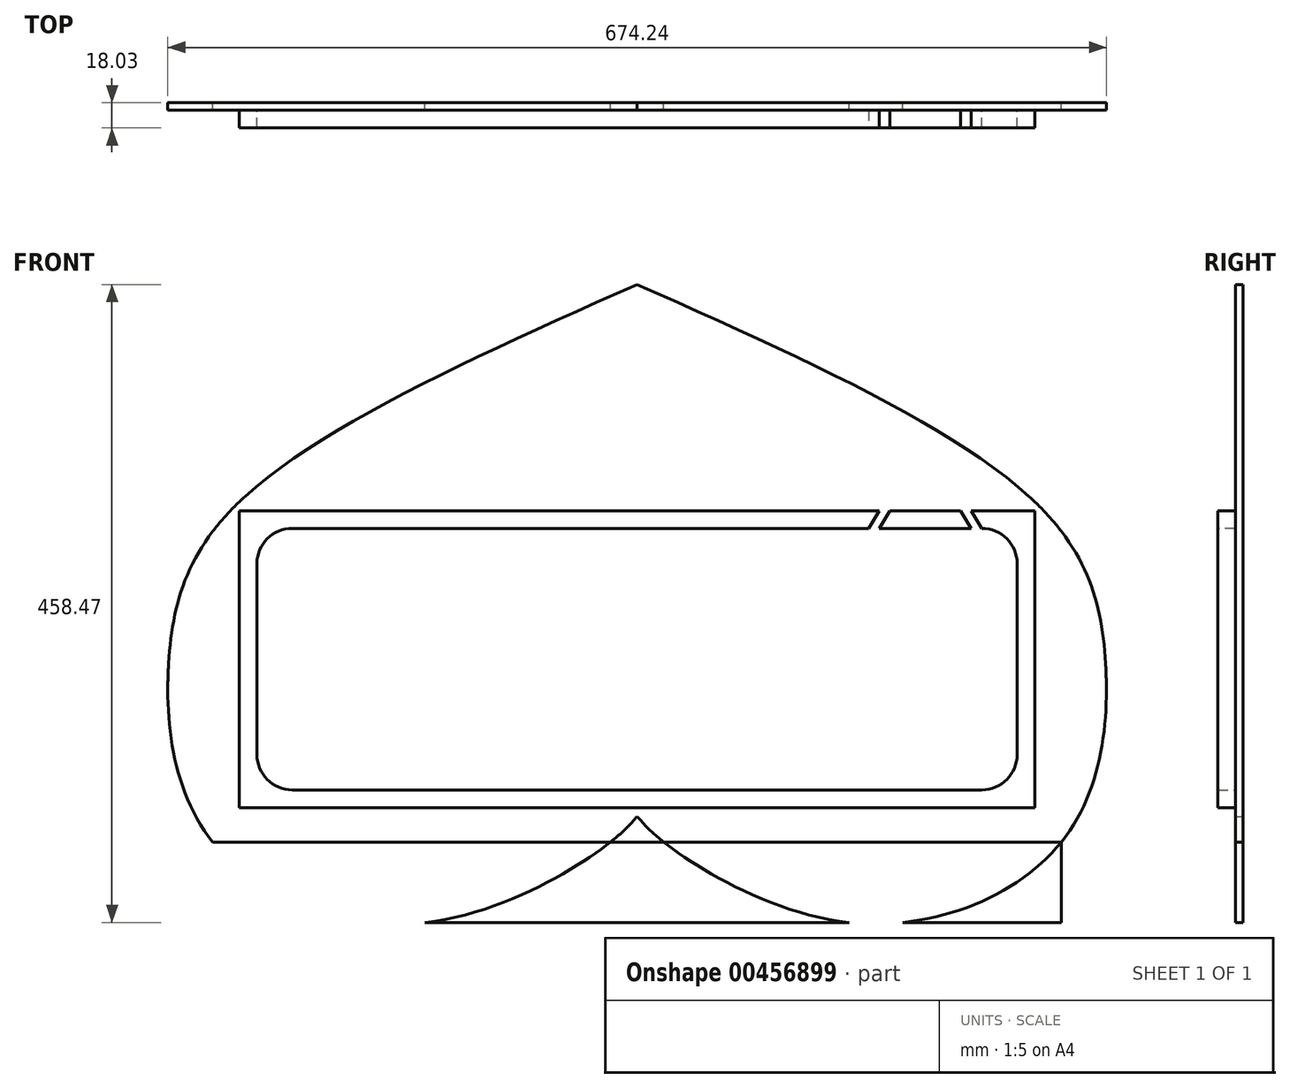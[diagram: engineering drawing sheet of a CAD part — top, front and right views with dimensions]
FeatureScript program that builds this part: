
annotation { "Feature Type Name" : "Feature", "Feature Type Description" : "" }
export const myFeature = defineFeature(function(context is Context, id is Id, definition is map)
    precondition{}
    {
        {
            var Q0;
            Q0=qCreatedBy(makeId("Front.planeOp"),FACE);
            var sketch = newSketch(context, id + "F0", { "sketchPlane" : qUnion([Q0])});
            skLineSegment(sketch, "E0.bottom", {"start": v(0, 0) * mm, "end": v(-584.2, 0) * mm});
            skLineSegment(sketch, "E0.top", {"start": v(0, 219.7) * mm, "end": v(-584.2, 219.7) * mm});
            skLineSegment(sketch, "E0.left", {"start": v(0, 0) * mm, "end": v(0, 219.7) * mm});
            skLineSegment(sketch, "E0.right", {"start": v(-584.2, 0) * mm, "end": v(-584.2, 219.7) * mm});
            skPoint(sketch, "E1", {"position": v(-292.1, 219.7) * mm});
            skSolve(sketch);
        }
        {
            var Q0;
            Q0=makeQuery(id+"F0.imprint","IMPRINT",FACE,{"disambiguationData":[TD([[makeQuery(id+"F0.imprint","IMPRINT",EDGE,{"derivedFrom":sQuery(id+"F0.wireOp",EDGE,"E0.bottom")}),-1.0]])]});
            extrude(context, id + "F1", {"entities" : qUnion([Q0]), "depth" : 5.33 * mm});
        }
        {
            var Q0;
            Q0=makeQuery(id+"F1.opExtrude","CAP_FACE",FACE,{"disambiguationData":[OSD([sQuery(id+"F0.wireOp",EDGE,"E0.bottom"),sQuery(id+"F0.wireOp",EDGE,"E0.top"),sQuery(id+"F0.wireOp",EDGE,"E0.left"),sQuery(id+"F0.wireOp",EDGE,"E0.right")])],"isStart":false});
            var sketch = newSketch(context, id + "F2", { "sketchPlane" : qUnion([Q0])});
            skLineSegment(sketch, "E2", {"start": v(-577.85, 219.7) * mm, "end": v(-577.85, 6.35) * mm});
            skLineSegment(sketch, "E3", {"start": v(-577.85, 6.35) * mm, "end": v(-6.35, 6.35) * mm});
            skLineSegment(sketch, "E4", {"start": v(-6.35, 6.35) * mm, "end": v(-6.35, 219.71) * mm});
            skLineSegment(sketch, "E5", {"start": v(-6.35, 219.71) * mm, "end": v(-577.85, 219.7) * mm});
            skLineSegment(sketch, "E6", {"start": v(-565.15, 207) * mm, "end": v(-565.15, 19.05) * mm});
            skLineSegment(sketch, "E7", {"start": v(-565.15, 19.05) * mm, "end": v(-19.05, 19.05) * mm});
            skLineSegment(sketch, "E8", {"start": v(-19.05, 19.05) * mm, "end": v(-19.05, 207.01) * mm});
            skLineSegment(sketch, "E9", {"start": v(-19.05, 207.01) * mm, "end": v(-565.15, 207) * mm});
            skSolve(sketch);
        }
        {
            var Q0;
            Q0=makeQuery(id+"F2.imprint","IMPRINT",FACE,{"disambiguationData":[TD([[makeQuery(id+"F2.imprint","IMPRINT",EDGE,{"derivedFrom":sQuery(id+"F2.wireOp",EDGE,"E2")}),1.0]])]});
            extrude(context, id + "F3", {"entities" : qUnion([Q0]), "operationType" : NewBodyOperationType.ADD, "depth" : 12.7 * mm});
        }
        {
            var Q0;
            Q0=makeQuery(id+"F3.opExtrude","SWEPT_EDGE",EDGE,{"disambiguationData":[OSD([sQuery(id+"F2.wireOp",EDGE,"E6"),sQuery(id+"F2.wireOp",EDGE,"E9")])]});
            var Q1;
            Q1=makeQuery(id+"F3.opExtrude","SWEPT_EDGE",EDGE,{"disambiguationData":[OSD([sQuery(id+"F2.wireOp",EDGE,"E8"),sQuery(id+"F2.wireOp",EDGE,"E9")])]});
            var Q2;
            Q2=makeQuery(id+"F3.opExtrude","SWEPT_EDGE",EDGE,{"disambiguationData":[OSD([sQuery(id+"F2.wireOp",EDGE,"E7"),sQuery(id+"F2.wireOp",EDGE,"E8")])]});
            var Q3;
            Q3=makeQuery(id+"F3.opExtrude","SWEPT_EDGE",EDGE,{"disambiguationData":[OSD([sQuery(id+"F2.wireOp",EDGE,"E6"),sQuery(id+"F2.wireOp",EDGE,"E7")])]});
            fillet(context, id + "F4", {"entities" : qUnion([Q0, Q1, Q2, Q3]), "radius" : 25.4 * mm, "tangentPropagation" : true, "allowEdgeOverflow" : false});
        }
        {
            var Q0;
            Q0=makeQuery(id+"F3.opExtrude","CAP_FACE",FACE,{"disambiguationData":[OSD([sQuery(id+"F2.wireOp",EDGE,"E2"),sQuery(id+"F2.wireOp",EDGE,"E3"),sQuery(id+"F2.wireOp",EDGE,"E4"),sQuery(id+"F2.wireOp",EDGE,"E5"),sQuery(id+"F2.wireOp",EDGE,"E6"),sQuery(id+"F2.wireOp",EDGE,"E7"),sQuery(id+"F2.wireOp",EDGE,"E8"),sQuery(id+"F2.wireOp",EDGE,"E9")])],"isStart":false});
            var sketch = newSketch(context, id + "F5", { "sketchPlane" : qUnion([Q0])});
            skPoint(sketch, "E10", {"position": v(-118.11, 219.7) * mm});
            skPoint(sketch, "E11", {"position": v(-110.5, 219.7) * mm});
            skPoint(sketch, "E12", {"position": v(-59.69, 219.7) * mm});
            skPoint(sketch, "E13", {"position": v(-52.07, 219.7) * mm});
            skPoint(sketch, "E14", {"position": v(-376.28, 272.75) * mm});
            skPoint(sketch, "E15", {"position": v(-12.7, 0) * mm});
            skPoint(sketch, "E16", {"position": v(-20.32, 0) * mm});
            skLineSegment(sketch, "E17", {"start": v(-20.32, 0) * mm, "end": v(-12.7, 0) * mm});
            skPoint(sketch, "E18", {"position": v(-118.11, 207.01) * mm});
            skPoint(sketch, "E19", {"position": v(-125.73, 207.01) * mm});
            skLineSegment(sketch, "E20", {"start": v(-125.73, 207.01) * mm, "end": v(-118.11, 219.7) * mm});
            skLineSegment(sketch, "E21", {"start": v(-125.73, 207.01) * mm, "end": v(-118.11, 207.01) * mm});
            skLineSegment(sketch, "E22", {"start": v(-118.11, 207.01) * mm, "end": v(-110.5, 219.7) * mm});
            skLineSegment(sketch, "E23", {"start": v(-118.11, 219.7) * mm, "end": v(-110.5, 219.7) * mm});
            skLineSegment(sketch, "E24", {"start": v(-59.69, 219.7) * mm, "end": v(-52.07, 219.7) * mm});
            skLineSegment(sketch, "E25", {"start": v(-110.5, 219.7) * mm, "end": v(-59.69, 219.7) * mm});
            skLineSegment(sketch, "E26", {"start": v(-59.69, 219.7) * mm, "end": v(-110.5, 219.7) * mm});
            skLineSegment(sketch, "E27", {"start": v(-110.5, 219.7) * mm, "end": v(-113.58, 214.56) * mm});
            skPoint(sketch, "E28", {"position": v(-44.45, 207.01) * mm});
            skPoint(sketch, "E29", {"position": v(-52.07, 207.01) * mm});
            skLineSegment(sketch, "E30", {"start": v(-59.69, 219.7) * mm, "end": v(-52.07, 207.01) * mm});
            skLineSegment(sketch, "E31", {"start": v(-52.07, 219.7) * mm, "end": v(-44.45, 207.01) * mm});
            skLineSegment(sketch, "E32", {"start": v(-52.07, 207.01) * mm, "end": v(-44.45, 207.01) * mm});
            skLineSegment(sketch, "E33", {"start": v(-52.07, 219.7) * mm, "end": v(-59.69, 219.7) * mm});
            skPoint(sketch, "E34", {"position": v(-56.6, 214.56) * mm});
            skLineSegment(sketch, "E35", {"start": v(-113.58, 214.56) * mm, "end": v(-56.6, 214.56) * mm});
            skSolve(sketch);
        }
        {
            var Q0;
            Q0=makeQuery(id+"F5.imprint","IMPRINT",FACE,{"disambiguationData":[TD([[makeQuery(id+"F5.imprint","IMPRINT",EDGE,{"derivedFrom":sQuery(id+"F5.wireOp",EDGE,"E20")}),-1.0]])]});
            var Q1;
            {var subQ8=sQuery(id+"F5.wireOp",EDGE,"RZINdJYM-ykuw-GilU-JIjt-DnibDYUsXZuo");Q1=makeQuery(id+"F5.imprint","IMPRINT",FACE,{"disambiguationData":[TD([[makeQuery(id+"F5.imprint","IMPRINT",EDGE,{"derivedFrom":subQ8}),1.0]])]});}
            var Q2;
            Q2=makeQuery(id+"F5.imprint","IMPRINT",FACE,{"disambiguationData":[TD([[makeQuery(id+"F5.imprint","IMPRINT",EDGE,{"derivedFrom":sQuery(id+"F5.wireOp",EDGE,"RZINdJYM-ykuw-GilU-JIjt-DnibDYUsXZuo")}),-1.0]])]});
            var Q3;
            Q3=makeQuery(id+"F5.imprint","IMPRINT",FACE,{"disambiguationData":[TD([[makeQuery(id+"F5.imprint","IMPRINT",EDGE,{"derivedFrom":sQuery(id+"F5.wireOp",EDGE,"NQJIxGkc-Vixr-o2zM-VUe3-bVQ5EoZFKsab")}),1.0]])]});
            var Q4;
            Q4=makeQuery(id+"F5.imprint","IMPRINT",FACE,{"disambiguationData":[TD([[makeQuery(id+"F5.imprint","IMPRINT",EDGE,{"derivedFrom":sQuery(id+"F5.wireOp",EDGE,"E30")}),1.0]])]});
            var Q5;
            {var subQ0=sQuery(id+"F5.wireOp",EDGE,"E26");Q5=makeQuery(id+"F5.imprint","IMPRINT",FACE,{"disambiguationData":[TD([[makeQuery(id+"F5.imprint","IMPRINT",EDGE,{"derivedFrom":subQ0}),1.0]])]});}
            extrude(context, id + "F6", {"entities" : qUnion([Q0, Q1, Q2, Q3, Q4, Q5]), "operationType" : NewBodyOperationType.REMOVE, "oppositeDirection" : true, "depth" : 12.7 * mm});
        }
        {
            var Q0;
            Q0=makeQuery(id+"F1.opExtrude","CAP_FACE",FACE,{"disambiguationData":[OSD([sQuery(id+"F0.wireOp",EDGE,"E0.bottom"),sQuery(id+"F0.wireOp",EDGE,"E0.top"),sQuery(id+"F0.wireOp",EDGE,"E0.left"),sQuery(id+"F0.wireOp",EDGE,"E0.right")])],"isStart":true});
            var sketch = newSketch(context, id + "F7", { "sketchPlane" : qUnion([Q0])});
            skLineSegment(sketch, "E36", {"start": v(0, 0) * mm, "end": v(-12.7, 0) * mm});
            skLineSegment(sketch, "E37", {"start": v(-12.7, 0) * mm, "end": v(-12.7, 229.87) * mm});
            skLineSegment(sketch, "E38", {"start": v(-12.7, 229.87) * mm, "end": v(596.9, 229.87) * mm});
            skLineSegment(sketch, "E39", {"start": v(596.9, 229.87) * mm, "end": v(596.9, 0) * mm});
            skLineSegment(sketch, "E40", {"start": v(596.9, 0) * mm, "end": v(584.2, 0) * mm});
            skPoint(sketch, "E41", {"position": v(596.9, 114.93) * mm});
            skPoint(sketch, "E42", {"position": v(584.2, 109.85) * mm});
            skPoint(sketch, "E43", {"position": v(292.1, 229.87) * mm});
            skPoint(sketch, "E44", {"position": v(292.1, 219.7) * mm});
            skPoint(sketch, "E45", {"position": v(-12.7, 114.93) * mm});
            skPoint(sketch, "E46", {"position": v(0, 109.85) * mm});
            skPoint(sketch, "E47", {"position": v(546.1, 229.87) * mm});
            skPoint(sketch, "E48", {"position": v(38.1, 229.87) * mm});
            skPoint(sketch, "E49", {"position": v(-12.7, 191.77) * mm});
            skPoint(sketch, "E50", {"position": v(596.9, 191.77) * mm});
            skPoint(sketch, "E51", {"position": v(584.2, 183.25) * mm});
            skPoint(sketch, "E52", {"position": v(0, 176.13) * mm});
            skPoint(sketch, "E53", {"position": v(596.9, 63.5) * mm});
            skPoint(sketch, "E54", {"position": v(-12.7, 63.5) * mm});
            skPoint(sketch, "E55", {"position": v(0, 219.7) * mm});
            skPoint(sketch, "E56", {"position": v(584.2, 219.7) * mm});
            skPoint(sketch, "E57", {"position": v(393.7, 219.7) * mm});
            skPoint(sketch, "E58", {"position": v(190.5, 219.7) * mm});
            skLineSegment(sketch, "E59", {"start": v(292.1, 219.7) * mm, "end": v(-12.7, 229.87) * mm});
            skLineSegment(sketch, "E60", {"start": v(292.1, 219.7) * mm, "end": v(596.9, 229.87) * mm});
            skLineSegment(sketch, "E61", {"start": v(596.9, -18.42) * mm, "end": v(-12.7, -18.42) * mm});
            skLineSegment(sketch, "E62", {"start": v(596.9, 0) * mm, "end": v(596.9, -18.42) * mm});
            skLineSegment(sketch, "E63", {"start": v(292.1, 229.87) * mm, "end": v(292.1, 382.27) * mm});
            skPoint(sketch, "E64", {"position": v(292.1, -18.42) * mm});
            skLineSegment(sketch, "E65", {"start": v(596.9, -18.42) * mm, "end": v(596.9, -76.2) * mm});
            skLineSegment(sketch, "E66", {"start": v(596.9, -76.2) * mm, "end": v(292.1, -76.2) * mm});
            skPoint(sketch, "E67", {"position": v(292.1, 0) * mm});
            skPoint(sketch, "E68", {"position": v(444.5, -76.2) * mm});
            skLineSegment(sketch, "E69", {"start": v(292.1, -76.2) * mm, "end": v(-12.7, -76.2) * mm});
            skLineSegment(sketch, "E70", {"start": v(-12.7, -76.2) * mm, "end": v(-12.7, -18.42) * mm});
            skPoint(sketch, "E71", {"position": v(139.7, -76.2) * mm});
            skPoint(sketch, "E72", {"position": v(571.5, -18.42) * mm});
            skPoint(sketch, "E73", {"position": v(12.7, -18.42) * mm});
            skPoint(sketch, "E74", {"position": v(6.35, 219.7) * mm});
            skPoint(sketch, "E75", {"position": v(577.85, 219.7) * mm});
            skPoint(sketch, "E76", {"position": v(6.35, 0) * mm});
            skPoint(sketch, "E77", {"position": v(577.85, 0) * mm});
            skPoint(sketch, "E78", {"position": v(69.85, 229.87) * mm});
            skPoint(sketch, "E79", {"position": v(514.35, 229.87) * mm});
            skLineSegment(sketch, "E80", {"start": v(69.85, 229.87) * mm, "end": v(69.85, 267.97) * mm});
            skLineSegment(sketch, "E81", {"start": v(514.35, 229.87) * mm, "end": v(514.35, 267.97) * mm});
            skLineSegment(sketch, "E82", {"start": v(292.1, 0) * mm, "end": v(292.1, 6.35) * mm});
            skPoint(sketch, "E83", {"position": v(311.15, -18.42) * mm});
            skPoint(sketch, "E84", {"position": v(273.05, -18.42) * mm});
            skLineSegment(sketch, "E85", {"start": v(0, 109.85) * mm, "end": v(-44.45, 109.85) * mm});
            skLineSegment(sketch, "E86", {"start": v(584.2, 109.85) * mm, "end": v(628.65, 109.85) * mm});
            skLineSegment(sketch, "E87", {"start": v(-44.45, 109.85) * mm, "end": v(-44.45, 84.45) * mm});
            skLineSegment(sketch, "E88", {"start": v(-12.7, 0) * mm, "end": v(-12.7, -18.42) * mm});
            skLineSegment(sketch, "E89", {"start": v(628.65, 109.85) * mm, "end": v(628.65, 84.45) * mm});
            skFitSpline(sketch, "E90", {"points": [v(292.1, 0) * mm, v(273.05, -18.42) * mm, v(139.7, -76.2) * mm, v(-12.7, -18.42) * mm, v(-44.45, 109.85) * mm, v(0, 219.7) * mm, v(292.1, 382.27) * mm], "startDerivative": vector(-185.21, -216.1) * mm, "endDerivative": vector(1377.2, 612.59) * mm});
            skFitSpline(sketch, "E91", {"points": [v(292.1, 0) * mm, v(311.15, -18.42) * mm, v(444.5, -76.2) * mm, v(596.9, -18.42) * mm, v(628.65, 109.85) * mm, v(584.2, 219.7) * mm, v(292.1, 382.27) * mm], "startDerivative": vector(185.21, -216.1) * mm, "endDerivative": vector(-1377.2, 612.59) * mm});
            skLineSegment(sketch, "E92", {"start": v(629.22, 167.92) * mm, "end": v(629.22, 51.7) * mm});
            skLineSegment(sketch, "E93", {"start": v(-45.02, 186.81) * mm, "end": v(-45.02, 61.14) * mm});
            skSolve(sketch);
        }
        {
            var Q0;
            {var subQ0=sQuery(id+"F7.wireOp",EDGE,"E63");Q0=makeQuery(id+"F7.imprint","IMPRINT",FACE,{"disambiguationData":[TD([[makeQuery(id+"F7.imprint","IMPRINT",EDGE,{"derivedFrom":subQ0}),-1.0]])]});}
            var Q1;
            {var subQ0=sQuery(id+"F7.wireOp",EDGE,"E63");Q1=makeQuery(id+"F7.imprint","IMPRINT",FACE,{"disambiguationData":[TD([[makeQuery(id+"F7.imprint","IMPRINT",EDGE,{"derivedFrom":subQ0}),1.0]])]});}
            var Q2;
            {var subQ0=sQuery(id+"F7.wireOp",EDGE,"E80");Q2=makeQuery(id+"F7.imprint","IMPRINT",FACE,{"disambiguationData":[TD([[makeQuery(id+"F7.imprint","IMPRINT",EDGE,{"derivedFrom":subQ0}),1.0]])]});}
            var Q3;
            {var subQ0=sQuery(id+"F7.wireOp",EDGE,"E38");var subQ5=makeQuery(id+"F7.imprint","INTERSECT",VERTEX,{"derivedFrom":[subQ0,sQuery(id+"F7.wireOp",EDGE,"E80")]});Q3=makeQuery(id+"F7.imprint","IMPRINT",FACE,{"disambiguationData":[TD([[makeQuery(id+"F7.imprint","IMPRINT",EDGE,{"disambiguationData":[TD([[subQ5,1.0]])],"derivedFrom":subQ0}),-1.0]])]});}
            var Q4;
            {var subQ0=sQuery(id+"F7.wireOp",EDGE,"E59");var subQ3=sQuery(id+"F7.wireOp",EDGE,"71ab5504-d169-43ff-8b42-9dfc2ffe11ae");var subQ4=makeQuery(id+"F7.imprint","INTERSECT",VERTEX,{"derivedFrom":[subQ0,subQ3]});Q4=makeQuery(id+"F7.imprint","IMPRINT",FACE,{"disambiguationData":[TD([[makeQuery(id+"F7.imprint","IMPRINT",EDGE,{"disambiguationData":[TD([[subQ4,1.0]])],"derivedFrom":subQ0}),1.0]])]});}
            var Q5;
            {var subQ0=sQuery(id+"F7.wireOp",EDGE,"71ab5504-d169-43ff-8b42-9dfc2ffe11ae");var subQ1=sQuery(id+"F7.wireOp",EDGE,"E37");var subQ2=makeQuery(id+"F7.imprint","INTERSECT",VERTEX,{"derivedFrom":[subQ1,subQ0]});Q5=makeQuery(id+"F7.imprint","IMPRINT",FACE,{"disambiguationData":[TD([[makeQuery(id+"F7.imprint","IMPRINT",EDGE,{"disambiguationData":[TD([[subQ2,1.0]])],"derivedFrom":subQ1}),-1.0]])]});}
            var Q6;
            {var subQ0=sQuery(id+"F7.wireOp",EDGE,"71ab5504-d169-43ff-8b42-9dfc2ffe11ae");var subQ1=sQuery(id+"F7.wireOp",EDGE,"E37");var subQ2=makeQuery(id+"F7.imprint","INTERSECT",VERTEX,{"derivedFrom":[subQ1,subQ0]});Q6=makeQuery(id+"F7.imprint","IMPRINT",FACE,{"disambiguationData":[TD([[makeQuery(id+"F7.imprint","IMPRINT",EDGE,{"disambiguationData":[TD([[subQ2,1.0]])],"derivedFrom":subQ1}),1.0]])]});}
            var Q7;
            {var subQ0=sQuery(id+"F7.wireOp",EDGE,"E36");Q7=makeQuery(id+"F7.imprint","IMPRINT",FACE,{"disambiguationData":[TD([[makeQuery(id+"F7.imprint","IMPRINT",EDGE,{"derivedFrom":subQ0}),-1.0]])]});}
            var Q8;
            {var subQ0=sQuery(id+"F7.wireOp",EDGE,"E88");Q8=makeQuery(id+"F7.imprint","IMPRINT",FACE,{"disambiguationData":[TD([[makeQuery(id+"F7.imprint","IMPRINT",EDGE,{"derivedFrom":subQ0}),-1.0]])]});}
            var Q9;
            {var subQ0=sQuery(id+"F7.wireOp",EDGE,"71ab5504-d169-43ff-8b42-9dfc2ffe11ae");var subQ4=sQuery(id+"F7.wireOp",EDGE,"E69");var subQ5=makeQuery(id+"F7.imprint","INTERSECT",VERTEX,{"disambiguationData":[OD(0.0)],"derivedFrom":[subQ4,subQ0]});Q9=makeQuery(id+"F7.imprint","IMPRINT",FACE,{"disambiguationData":[TD([[makeQuery(id+"F7.imprint","IMPRINT",EDGE,{"disambiguationData":[TD([[subQ5,-1.0]])],"derivedFrom":subQ4}),-1.0]])]});}
            var Q10;
            {var subQ6=sQuery(id+"F7.wireOp",EDGE,"E36");Q10=makeQuery(id+"F7.imprint","IMPRINT",FACE,{"disambiguationData":[TD([[makeQuery(id+"F7.imprint","IMPRINT",EDGE,{"derivedFrom":subQ6}),1.0]])]});}
            var Q11;
            {var subQ0=sQuery(id+"F7.wireOp",EDGE,"66e556fc-33cd-4848-b358-339aebe7346d");var subQ4=sQuery(id+"F7.wireOp",EDGE,"E66");var subQ5=makeQuery(id+"F7.imprint","INTERSECT",VERTEX,{"disambiguationData":[OD(0.0)],"derivedFrom":[subQ4,subQ0]});Q11=makeQuery(id+"F7.imprint","IMPRINT",FACE,{"disambiguationData":[TD([[makeQuery(id+"F7.imprint","IMPRINT",EDGE,{"disambiguationData":[TD([[subQ5,-1.0]])],"derivedFrom":subQ4}),-1.0]])]});}
            var Q12;
            {var subQ6=sQuery(id+"F7.wireOp",EDGE,"E40");Q12=makeQuery(id+"F7.imprint","IMPRINT",FACE,{"disambiguationData":[TD([[makeQuery(id+"F7.imprint","IMPRINT",EDGE,{"derivedFrom":subQ6}),1.0]])]});}
            var Q13;
            {var subQ5=sQuery(id+"F7.wireOp",EDGE,"E62");Q13=makeQuery(id+"F7.imprint","IMPRINT",FACE,{"disambiguationData":[TD([[makeQuery(id+"F7.imprint","IMPRINT",EDGE,{"derivedFrom":subQ5}),1.0]])]});}
            var Q14;
            {var subQ0=sQuery(id+"F7.wireOp",EDGE,"E40");Q14=makeQuery(id+"F7.imprint","IMPRINT",FACE,{"disambiguationData":[TD([[makeQuery(id+"F7.imprint","IMPRINT",EDGE,{"derivedFrom":subQ0}),-1.0]])]});}
            var Q15;
            {var subQ0=sQuery(id+"F7.wireOp",EDGE,"66e556fc-33cd-4848-b358-339aebe7346d");var subQ1=sQuery(id+"F7.wireOp",EDGE,"E39");var subQ2=makeQuery(id+"F7.imprint","INTERSECT",VERTEX,{"derivedFrom":[subQ1,subQ0]});Q15=makeQuery(id+"F7.imprint","IMPRINT",FACE,{"disambiguationData":[TD([[makeQuery(id+"F7.imprint","IMPRINT",EDGE,{"disambiguationData":[TD([[subQ2,-1.0]])],"derivedFrom":subQ1}),1.0]])]});}
            var Q16;
            {var subQ0=sQuery(id+"F7.wireOp",EDGE,"66e556fc-33cd-4848-b358-339aebe7346d");var subQ1=sQuery(id+"F7.wireOp",EDGE,"E39");var subQ2=makeQuery(id+"F7.imprint","INTERSECT",VERTEX,{"derivedFrom":[subQ1,subQ0]});Q16=makeQuery(id+"F7.imprint","IMPRINT",FACE,{"disambiguationData":[TD([[makeQuery(id+"F7.imprint","IMPRINT",EDGE,{"disambiguationData":[TD([[subQ2,-1.0]])],"derivedFrom":subQ1}),-1.0]])]});}
            var Q17;
            {var subQ0=sQuery(id+"F7.wireOp",EDGE,"E60");var subQ3=sQuery(id+"F7.wireOp",EDGE,"66e556fc-33cd-4848-b358-339aebe7346d");var subQ4=makeQuery(id+"F7.imprint","INTERSECT",VERTEX,{"derivedFrom":[subQ0,subQ3]});Q17=makeQuery(id+"F7.imprint","IMPRINT",FACE,{"disambiguationData":[TD([[makeQuery(id+"F7.imprint","IMPRINT",EDGE,{"disambiguationData":[TD([[subQ4,1.0]])],"derivedFrom":subQ0}),-1.0]])]});}
            var Q18;
            {var subQ0=sQuery(id+"F7.wireOp",EDGE,"E81");Q18=makeQuery(id+"F7.imprint","IMPRINT",FACE,{"disambiguationData":[TD([[makeQuery(id+"F7.imprint","IMPRINT",EDGE,{"derivedFrom":subQ0}),-1.0]])]});}
            var Q19;
            {var subQ0=sQuery(id+"F7.wireOp",EDGE,"E91");var subQ4=sQuery(id+"F7.wireOp",EDGE,"E66");var subQ5=makeQuery(id+"F7.imprint","INTERSECT",VERTEX,{"disambiguationData":[OD(0.0)],"derivedFrom":[subQ4,subQ0]});Q19=makeQuery(id+"F7.imprint","IMPRINT",FACE,{"disambiguationData":[TD([[makeQuery(id+"F7.imprint","IMPRINT",EDGE,{"disambiguationData":[TD([[subQ5,-1.0]])],"derivedFrom":subQ4}),-1.0]])]});}
            var Q20;
            {var subQ0=sQuery(id+"F7.wireOp",EDGE,"E90");var subQ4=sQuery(id+"F7.wireOp",EDGE,"E69");var subQ5=makeQuery(id+"F7.imprint","INTERSECT",VERTEX,{"disambiguationData":[OD(0.0)],"derivedFrom":[subQ4,subQ0]});Q20=makeQuery(id+"F7.imprint","IMPRINT",FACE,{"disambiguationData":[TD([[makeQuery(id+"F7.imprint","IMPRINT",EDGE,{"disambiguationData":[TD([[subQ5,-1.0]])],"derivedFrom":subQ4}),-1.0]])]});}
            extrude(context, id + "F8", {"entities" : qUnion([Q0, Q1, Q2, Q3, Q4, Q5, Q6, Q7, Q8, Q9, Q10, Q11, Q12, Q13, Q14, Q15, Q16, Q17, Q18, Q19, Q20]), "operationType" : NewBodyOperationType.ADD, "depth" : -5.33 * mm});
        }
    });
